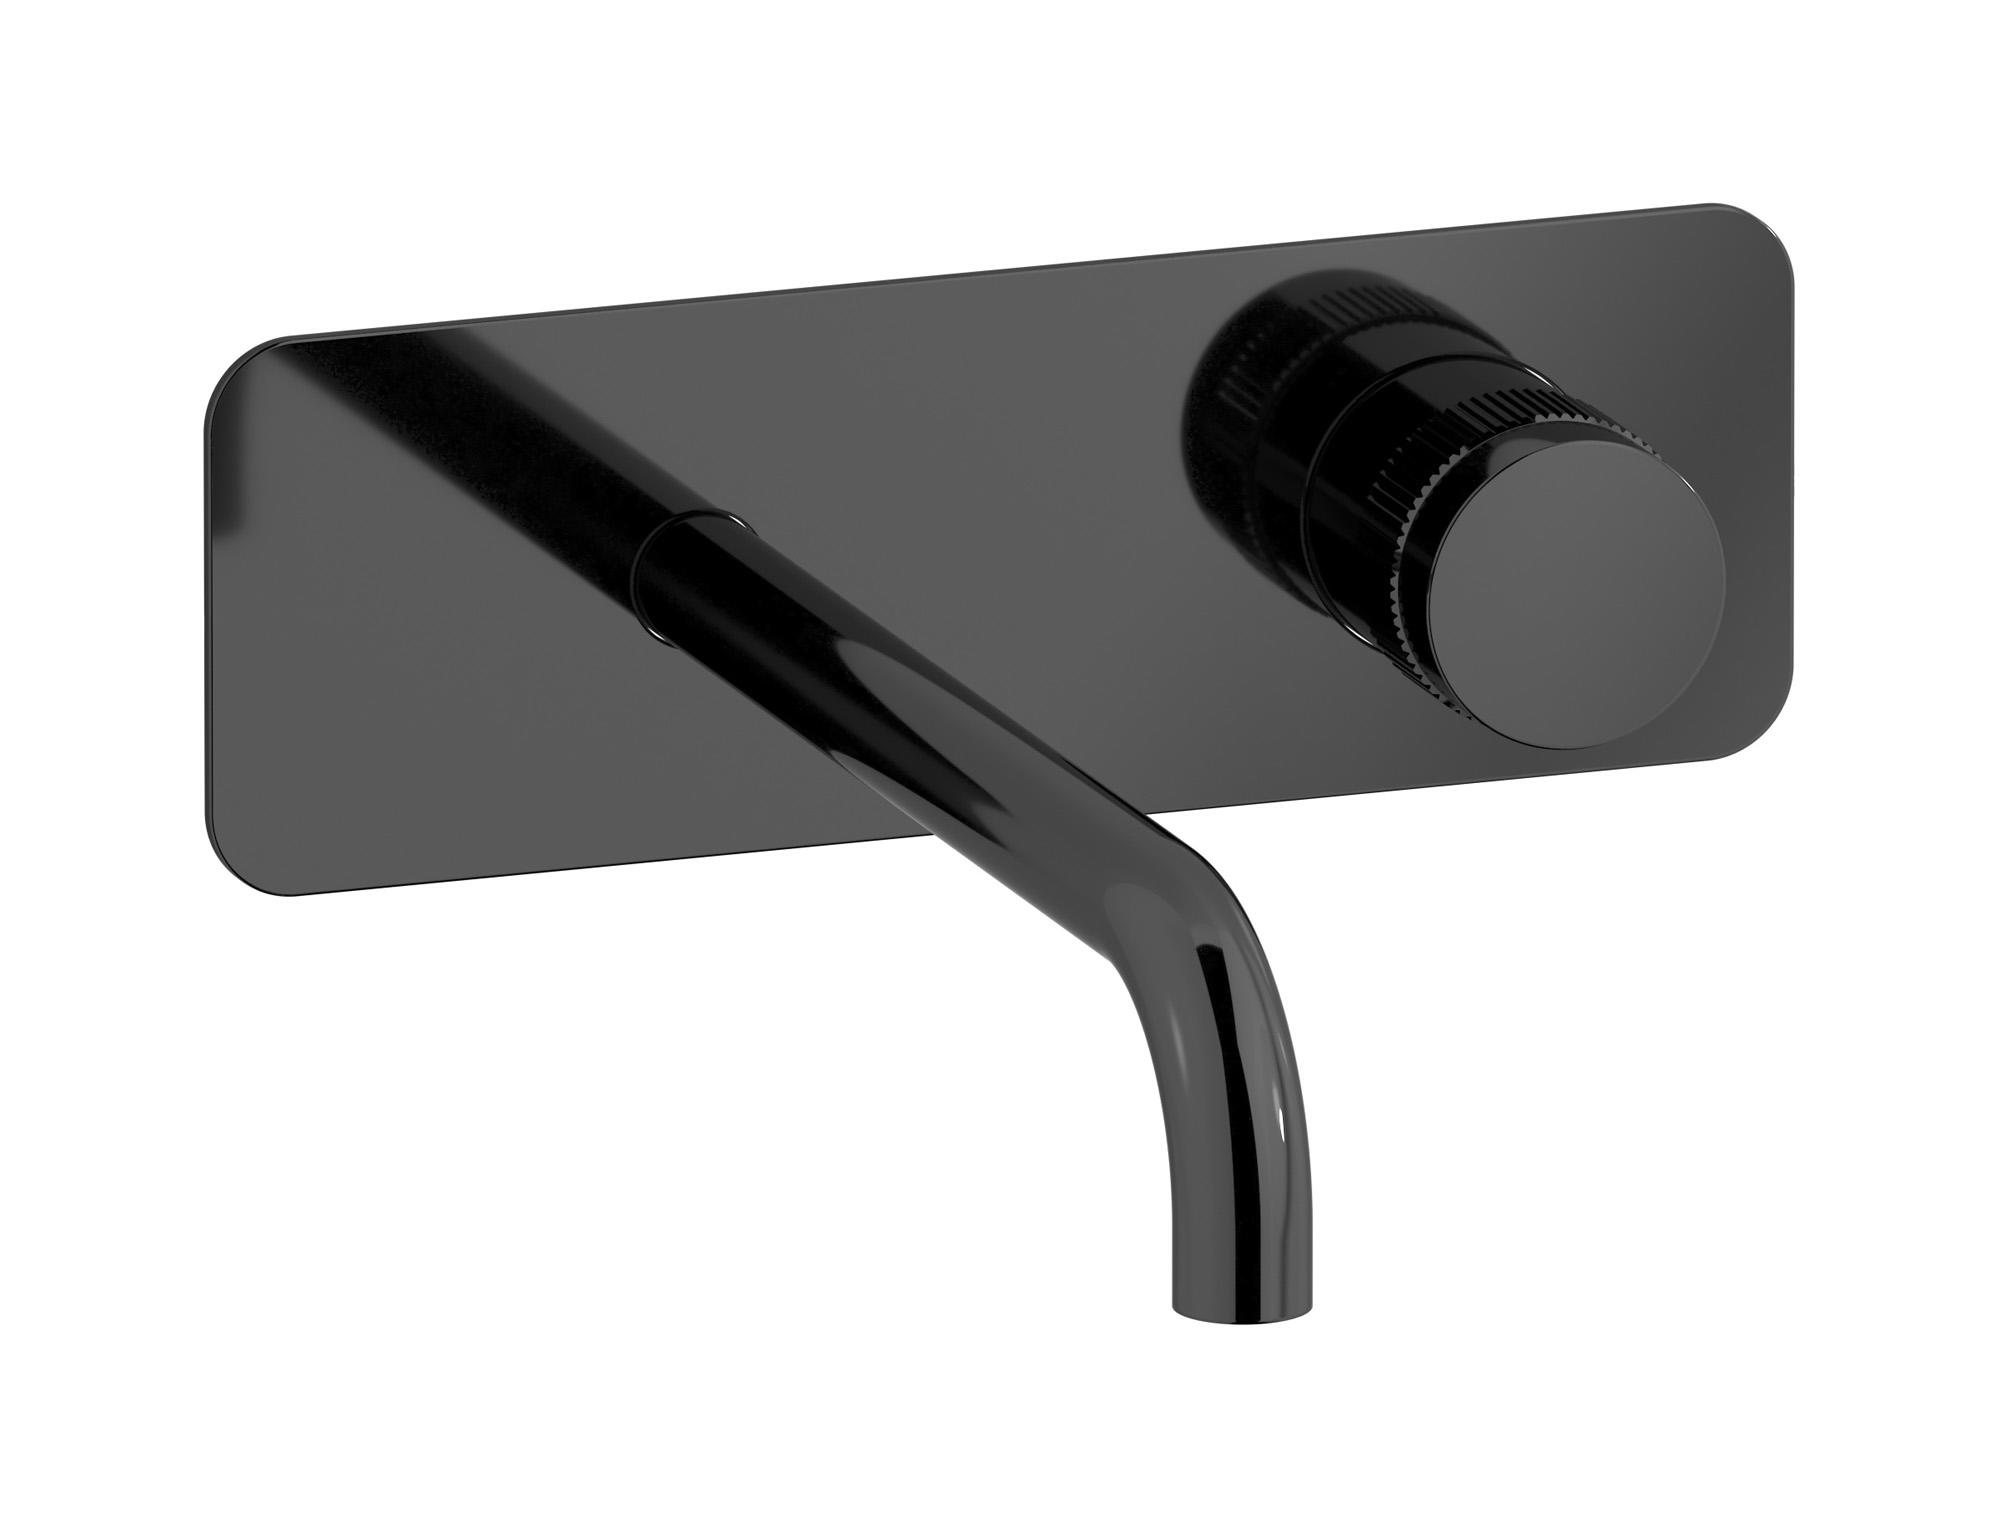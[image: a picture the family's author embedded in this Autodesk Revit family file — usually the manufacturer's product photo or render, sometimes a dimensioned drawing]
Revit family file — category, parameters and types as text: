
# Revit family: RX207
name_source: partatom
category: Apparecchi idraulici
units: mm (PartAtom-declared; Revit-internal decimal feet)

## family parameters
Basato su piano di lavoro = No
Condiviso = No
Mantieni orientamento annotazione = No
Numero OmniClass = 23.45.55.17
Punto di calcolo locali = No
Quota connettore circolare = Usa diametro
Sempre verticale = Sì
Taglio con vuoti quando caricato = No
Tipo di parte = Normale
Titolo OmniClass = Mixing Faucets

## types (12) — shared parameters
Cold water inlet = 10 mm  [stored 0.0328084 ft]
Commenti sul tipo = Wall monted washbasin hydroprogressive mixer with long spout complete
Connessione CW = No
Connessione HW = No
Connessione di scarico = No
Connessione di ventilazione = No
Descrizione = Wall monted washbasin hydroprogressive mixer with long spout complete
Hot water inlet = 10 mm  [stored 0.0328084 ft]
Produttore = IB Rubinetterie S.p.A.
URL = https://www.weareib.it
zero-valued in all types: Prospetto di default

## per-type parameters (varying)
| type | Finishes surface | Immagine tipo | Modello |
| Chrome | IB_Chrome | RX207CC.jpg | RX207CC |
| Black Chrome | IB_Black chrome | RX207CF.jpg | RX207CF |
| Brushed Black Chrome | IB_Brushed black chrome | RX207CS.jpg | RX207CS |
| Pale Gold | IB_Pale gold | RX207II.jpg | RX207II |
| Brushed Pale Gold | IB_brushed pale gold | RX207IS.jpg | RX207IS |
| Matt Black | IB_matt black | RX207NP.jpg | RX207NP |
| Natural Brass | IB_Brass | RX207ON.jpg | RX207ON |
| Gold | IB_gold | RX207OO.jpg | RX207OO |
| Brushed Gold | IB_brushed gold | RX207OS.jpg | RX207OS |
| Rose Gold | IB_Rose gold | RX207RS.jpg | RX207RS |
| Brushed Rose Gold | IB_Brushed rose gold | RX207SR.jpg | RX207SR |
| Brushed Nickel | IB_Brushed nickel | RX207SS.jpg | RX207SS |

note: [stored X ft] marks values corroborated as IEEE doubles in the binary element streams (Revit-internal decimal feet)
